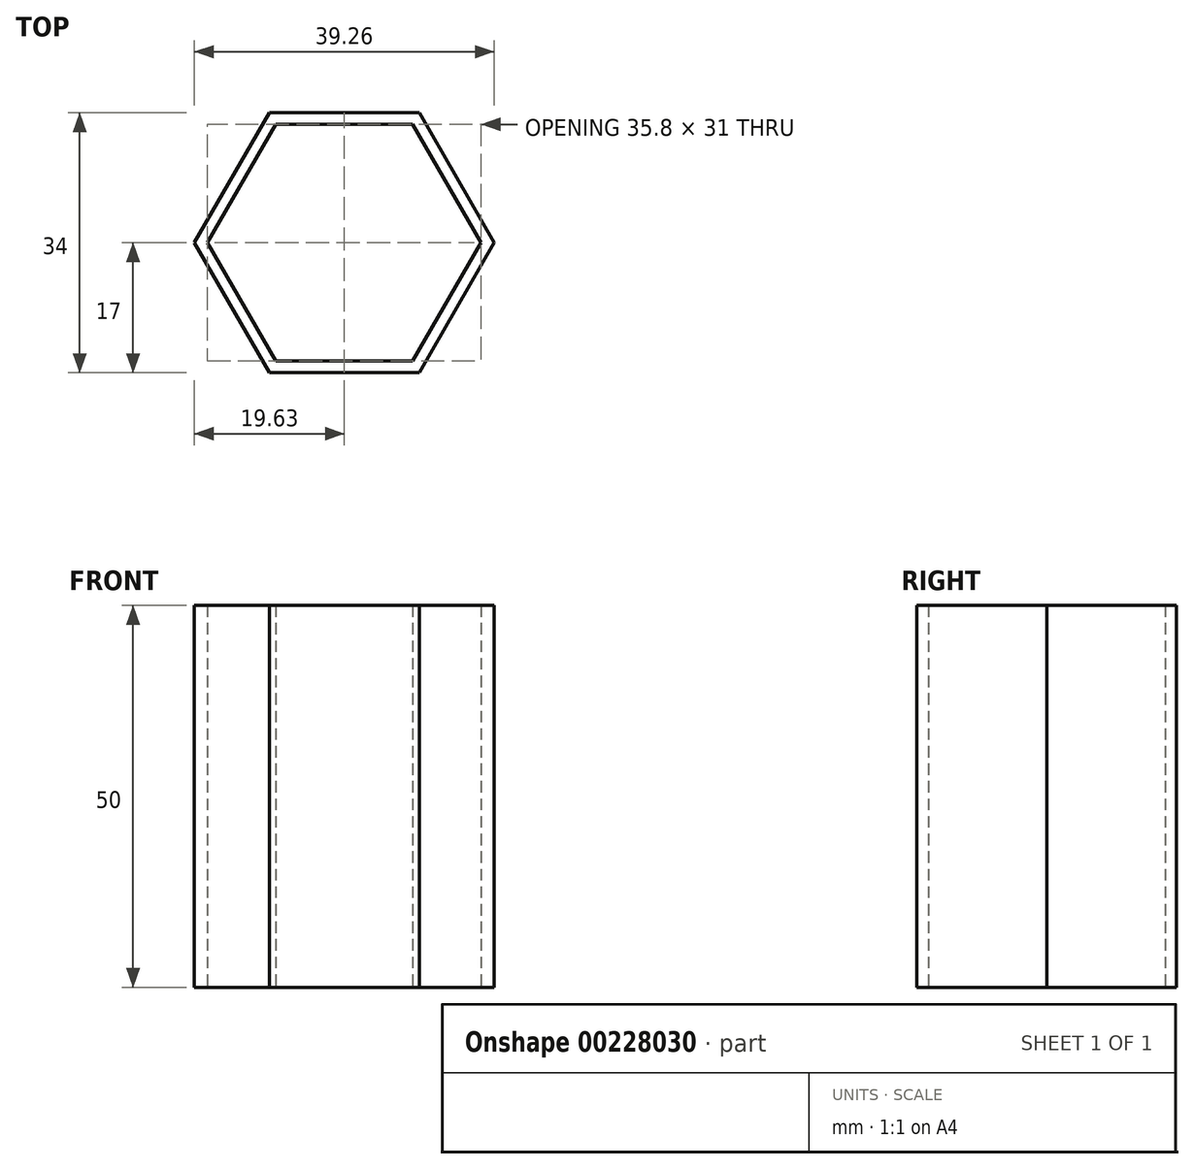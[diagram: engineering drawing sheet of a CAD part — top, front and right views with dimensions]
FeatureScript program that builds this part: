
annotation { "Feature Type Name" : "Feature", "Feature Type Description" : "" }
export const myFeature = defineFeature(function(context is Context, id is Id, definition is map)
    precondition{}
    {
        {
            var Q0;
            Q0=qCreatedBy(makeId("Top.planeOp"),FACE);
            var sketch = newSketch(context, id + "F0", { "sketchPlane" : qUnion([Q0])});
            skCircle(sketch, "E0.cCircle", {"center": v(0, 0) * mm, "radius": 17 * mm, "construction": true});
            skLineSegment(sketch, "E0.0", {"start": v(-9.81, 17) * mm, "end": v(9.81, 17) * mm});
            skLineSegment(sketch, "E0.1", {"start": v(9.81, 17) * mm, "end": v(19.63, 0) * mm});
            skLineSegment(sketch, "E0.2", {"start": v(19.63, 0) * mm, "end": v(9.81, -17) * mm});
            skLineSegment(sketch, "E0.3", {"start": v(9.81, -17) * mm, "end": v(-9.81, -17) * mm});
            skLineSegment(sketch, "E0.4", {"start": v(-9.81, -17) * mm, "end": v(-19.63, 0) * mm});
            skLineSegment(sketch, "E0.5", {"start": v(-19.63, 0) * mm, "end": v(-9.81, 17) * mm});
            skPoint(sketch, "E0.0.midPoint", {"position": v(0, 17) * mm});
            skCircle(sketch, "E1.cCircle", {"center": v(0, 0) * mm, "radius": 15.5 * mm, "construction": true});
            skLineSegment(sketch, "E1.0", {"start": v(-8.95, 15.5) * mm, "end": v(8.95, 15.5) * mm});
            skLineSegment(sketch, "E1.1", {"start": v(8.95, 15.5) * mm, "end": v(17.9, 0) * mm});
            skLineSegment(sketch, "E1.2", {"start": v(17.9, 0) * mm, "end": v(8.95, -15.5) * mm});
            skLineSegment(sketch, "E1.3", {"start": v(8.95, -15.5) * mm, "end": v(-8.95, -15.5) * mm});
            skLineSegment(sketch, "E1.4", {"start": v(-8.95, -15.5) * mm, "end": v(-17.9, 0) * mm});
            skLineSegment(sketch, "E1.5", {"start": v(-17.9, 0) * mm, "end": v(-8.95, 15.5) * mm});
            skPoint(sketch, "E1.0.midPoint", {"position": v(0, 15.5) * mm});
            skSolve(sketch);
        }
        {
            var Q0;
            Q0 = qSketchRegion(id + "F0", true);
            extrude(context, id + "F1", {"entities" : qUnion([Q0]), "depth" : 50 * mm});
        }
    });
